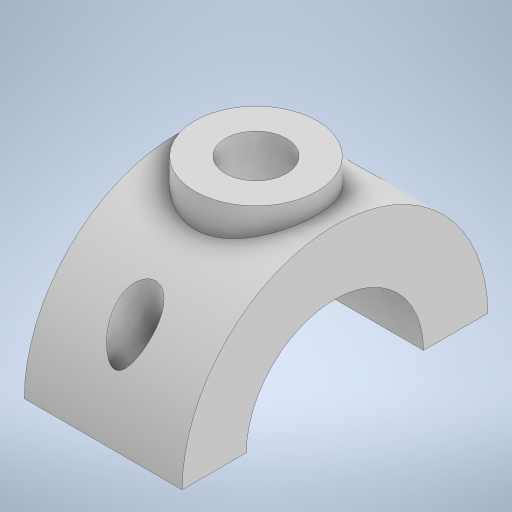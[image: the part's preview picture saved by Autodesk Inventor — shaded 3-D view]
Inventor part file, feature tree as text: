
AUTODESK INVENTOR PART (.ipt)
format: ipt  version: 2023 (Build 270158000, 158)  size: 297,472 bytes
history: native  units: mm
features: extrude x6, sketch x4, projected_geometry x4, plane x3
ambient origin geometry x8: Origin, YZ Plane, XZ Plane, XY Plane, X Axis, Y Axis, Z Axis, Center Point
bodies: Solid1 (feature_tree)
feature tree (17):
  extrude  "Extrusion1"  Depth=30.0mm
  plane  "Work Plane1"
  sketch  "Sketch2"  dims[d4=15.5mm d5=0.0mm d6=6.0mm]
  extrude  "Extrusion2"  Depth=6.0mm
  extrude  "Extrusion3"  Depth=15.5mm TaperAngle=0.0deg
  extrude  "Extrusion4"  TaperAngle=0.0deg  [1 undecoded]
  plane  "Work Plane2"
  extrude  "Extrusion5"  Depth=10.0mm
  plane  "Work Plane3"
  extrude  "Extrusion6"  Depth=10.0mm TaperAngle=0.0deg
  sketch  "Sketch1"  dims[d0=17.4mm d1=30.0mm]
  projected_geometry  "Projected Loop1"
  sketch  "Sketch3"  dims[d7=12.0mm d8=15.5mm d9=0.0mm]
  projected_geometry  "Projected Loop2"
  sketch  "Sketch4"  dims[d10=2.0mm d11=0.0mm d12=0.0mm d13=0.0mm d14=10.0mm d15=20.4mm d16=0.0mm d17=6.3mm d18=6.3mm d19=4.0mm d20=4.0mm d21=0.0mm d22=0.0mm]
  projected_geometry  "Projected Loop3"
  projected_geometry  "Projected Loop4"
note: 1 required parameter value undecoded (feature->parameter linkage not recoverable at this tier; creation-order binding heuristic only, values carry confidence <= 0.55)
